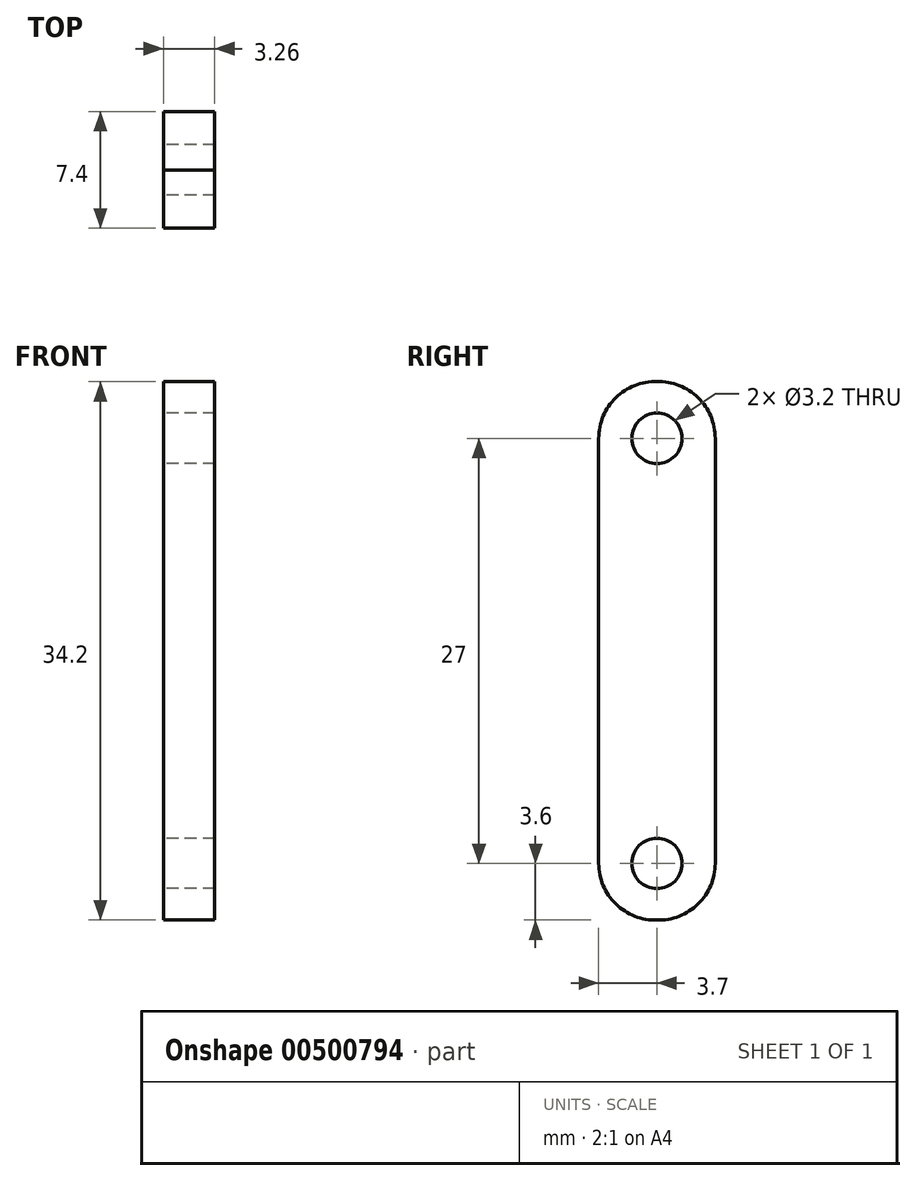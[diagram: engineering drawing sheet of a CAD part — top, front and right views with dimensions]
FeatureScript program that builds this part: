
annotation { "Feature Type Name" : "Feature", "Feature Type Description" : "" }
export const myFeature = defineFeature(function(context is Context, id is Id, definition is map)
    precondition{}
    {
        {
            var Q0;
            Q0=qCreatedBy(makeId("Right.planeOp"),FACE);
            var sketch = newSketch(context, id + "F0", { "sketchPlane" : qUnion([Q0])});
            skLineSegment(sketch, "E0.bottom", {"start": v(3.7, 13.5) * mm, "end": v(-3.7, 13.5) * mm});
            skLineSegment(sketch, "E0.top", {"start": v(3.7, -13.5) * mm, "end": v(-3.7, -13.5) * mm});
            skLineSegment(sketch, "E0.left", {"start": v(3.7, 13.5) * mm, "end": v(3.7, -13.5) * mm});
            skLineSegment(sketch, "E0.right", {"start": v(-3.7, 13.5) * mm, "end": v(-3.7, -13.5) * mm});
            skPoint(sketch, "E0.middle", {"position": v(0, 0) * mm});
            skLineSegment(sketch, "E1", {"start": v(0, 0) * mm, "end": v(0, 17.1) * mm});
            skPoint(sketch, "E1.endSnap0", {"position": v(0, 13.5) * mm});
            skLineSegment(sketch, "E2", {"start": v(0, 0) * mm, "end": v(0, -17.1) * mm});
            skPoint(sketch, "E2.endSnap0", {"position": v(0, -13.5) * mm});
            skArc(sketch, "E3", {"start": v(0, 17.1) * mm, "mid": v(-2.61, 16.08) * mm, "end": v(-3.7, 13.5) * mm});
            skArc(sketch, "E4", {"start": v(3.7, 13.5) * mm, "mid": v(2.61, 16.08) * mm, "end": v(0, 17.1) * mm});
            skArc(sketch, "E5", {"start": v(-3.7, -13.5) * mm, "mid": v(-2.61, -16.08) * mm, "end": v(0, -17.1) * mm});
            skArc(sketch, "E6", {"start": v(0, -17.1) * mm, "mid": v(2.61, -16.08) * mm, "end": v(3.7, -13.5) * mm});
            skCircle(sketch, "E7", {"center": v(0, 13.5) * mm, "radius": 1.6 * mm});
            skCircle(sketch, "E8", {"center": v(0, -13.5) * mm, "radius": 1.6 * mm});
            skPoint(sketch, "E9", {"position": v(0, 15.1) * mm});
            skPoint(sketch, "E10", {"position": v(0, -15.1) * mm});
            skSolve(sketch);
        }
        {
            var Q0;
            {var subQ0=sQuery(id+"F0.wireOp",EDGE,"E0.left");Q0=makeQuery(id+"F0.imprint","IMPRINT",FACE,{"disambiguationData":[TD([[makeQuery(id+"F0.imprint","IMPRINT",EDGE,{"derivedFrom":subQ0}),-1.0]])]});}
            var Q1;
            {var subQ5=sQuery(id+"F0.wireOp",EDGE,"E0.right");Q1=makeQuery(id+"F0.imprint","IMPRINT",FACE,{"disambiguationData":[TD([[makeQuery(id+"F0.imprint","IMPRINT",EDGE,{"derivedFrom":subQ5}),1.0]])]});}
            var Q2;
            {var subQ0=sQuery(id+"F0.wireOp",EDGE,"E3");Q2=makeQuery(id+"F0.imprint","IMPRINT",FACE,{"disambiguationData":[TD([[makeQuery(id+"F0.imprint","IMPRINT",EDGE,{"derivedFrom":subQ0}),1.0]])]});}
            var Q3;
            {var subQ0=sQuery(id+"F0.wireOp",EDGE,"E4");Q3=makeQuery(id+"F0.imprint","IMPRINT",FACE,{"disambiguationData":[TD([[makeQuery(id+"F0.imprint","IMPRINT",EDGE,{"derivedFrom":subQ0}),1.0]])]});}
            var Q4;
            {var subQ0=sQuery(id+"F0.wireOp",EDGE,"E6");Q4=makeQuery(id+"F0.imprint","IMPRINT",FACE,{"disambiguationData":[TD([[makeQuery(id+"F0.imprint","IMPRINT",EDGE,{"derivedFrom":subQ0}),1.0]])]});}
            var Q5;
            {var subQ0=sQuery(id+"F0.wireOp",EDGE,"E5");Q5=makeQuery(id+"F0.imprint","IMPRINT",FACE,{"disambiguationData":[TD([[makeQuery(id+"F0.imprint","IMPRINT",EDGE,{"derivedFrom":subQ0}),1.0]])]});}
            extrude(context, id + "F1", {"entities" : qUnion([Q0, Q1, Q2, Q3, Q4, Q5]), "depth" : 3.25 * mm, "offsetDistance" : 25 * mm, "symmetric" : true});
        }
    });
